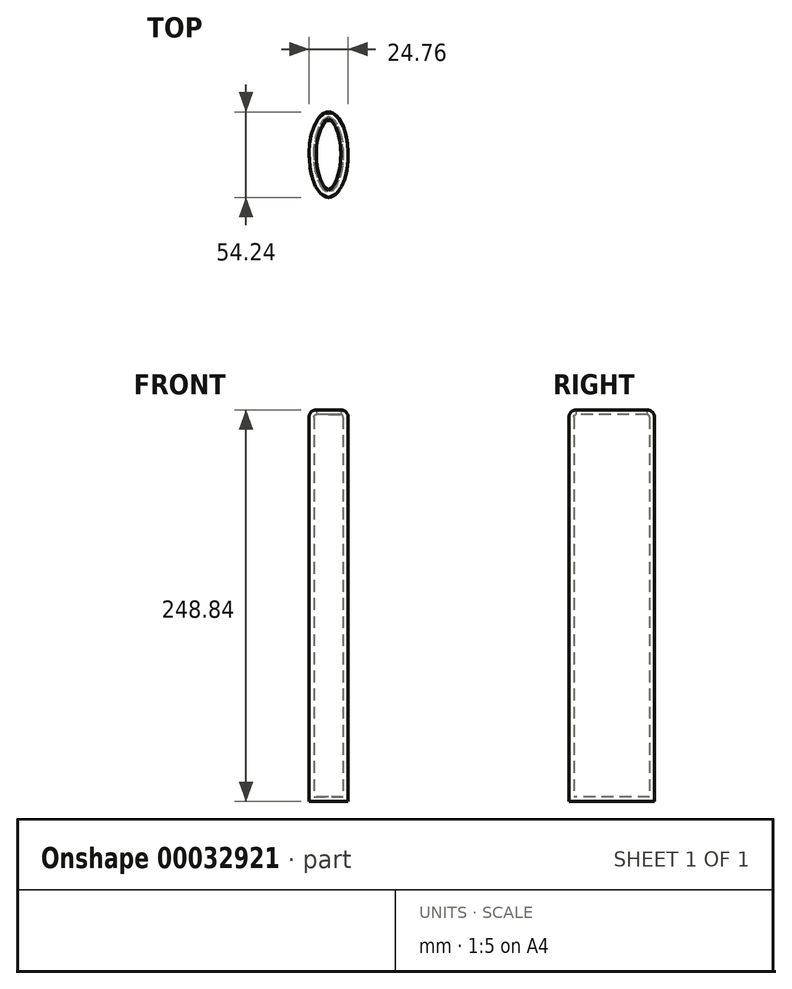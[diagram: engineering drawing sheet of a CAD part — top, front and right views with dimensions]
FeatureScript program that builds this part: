
annotation { "Feature Type Name" : "Feature", "Feature Type Description" : "" }
export const myFeature = defineFeature(function(context is Context, id is Id, definition is map)
    precondition{}
    {
        {
            var Q0;
            Q0=qCreatedBy(makeId("Top.planeOp"),FACE);
            var sketch = newSketch(context, id + "F0", { "sketchPlane" : qUnion([Q0])});
            skEllipse(sketch, "E0", {"center": v(0, 36.94) * mm, "majorRadius": 27.12 * mm, "minorRadius": 12.38 * mm, "majorAxis": v(0, -1)});
            skSolve(sketch);
        }
        {
            var Q0;
            Q0=makeQuery(id+"F0.imprint","IMPRINT",FACE,{"disambiguationData":[TD([[makeQuery(id+"F0.imprint","IMPRINT",EDGE,{"derivedFrom":sQuery(id+"F0.wireOp",EDGE,"E0")}),1.0]])]});
            extrude(context, id + "F1", {"entities" : qUnion([Q0]), "depth" : 248.84 * mm});
        }
        {
            var Q0;
            Q0=makeQuery(id+"F1.opExtrude","CAP_EDGE",EDGE,{"disambiguationData":[OSD([sQuery(id+"F0.wireOp",EDGE,"E0")])],"isStart":false});
            fillet(context, id + "F2", {"entities" : qUnion([Q0]), "radius" : 4.57 * mm, "tangentPropagation" : true, "allowEdgeOverflow" : false});
        }
        {
            var Q0;
            Q0=makeQuery(id+"F1.opExtrude","SWEPT_FACE",FACE,{"disambiguationData":[OSD([sQuery(id+"F0.wireOp",EDGE,"E0")])]});
            var Q1;
            Q1=makeQuery(id+"F1.opExtrude","SWEPT_BODY",BODY,{"disambiguationData":[OSD([sQuery(id+"F0.wireOp",EDGE,"E0")])]});
            shell(context, id + "F3", {"isHollow" : true, "entities" : qUnion([Q0]), "parts" : qUnion([Q1]), "thickness" : 3.05 * mm});
        }
        {
            var Q0;
            Q0=makeQuery(id+"F1.opExtrude","CAP_FACE",FACE,{"disambiguationData":[OSD([sQuery(id+"F0.wireOp",EDGE,"E0")])],"isStart":false});
            extrude(context, id + "F4", {"entities" : qUnion([Q0]), "operationType" : NewBodyOperationType.REMOVE, "oppositeDirection" : true, "depth" : 87.88 * mm});
        }
    });
